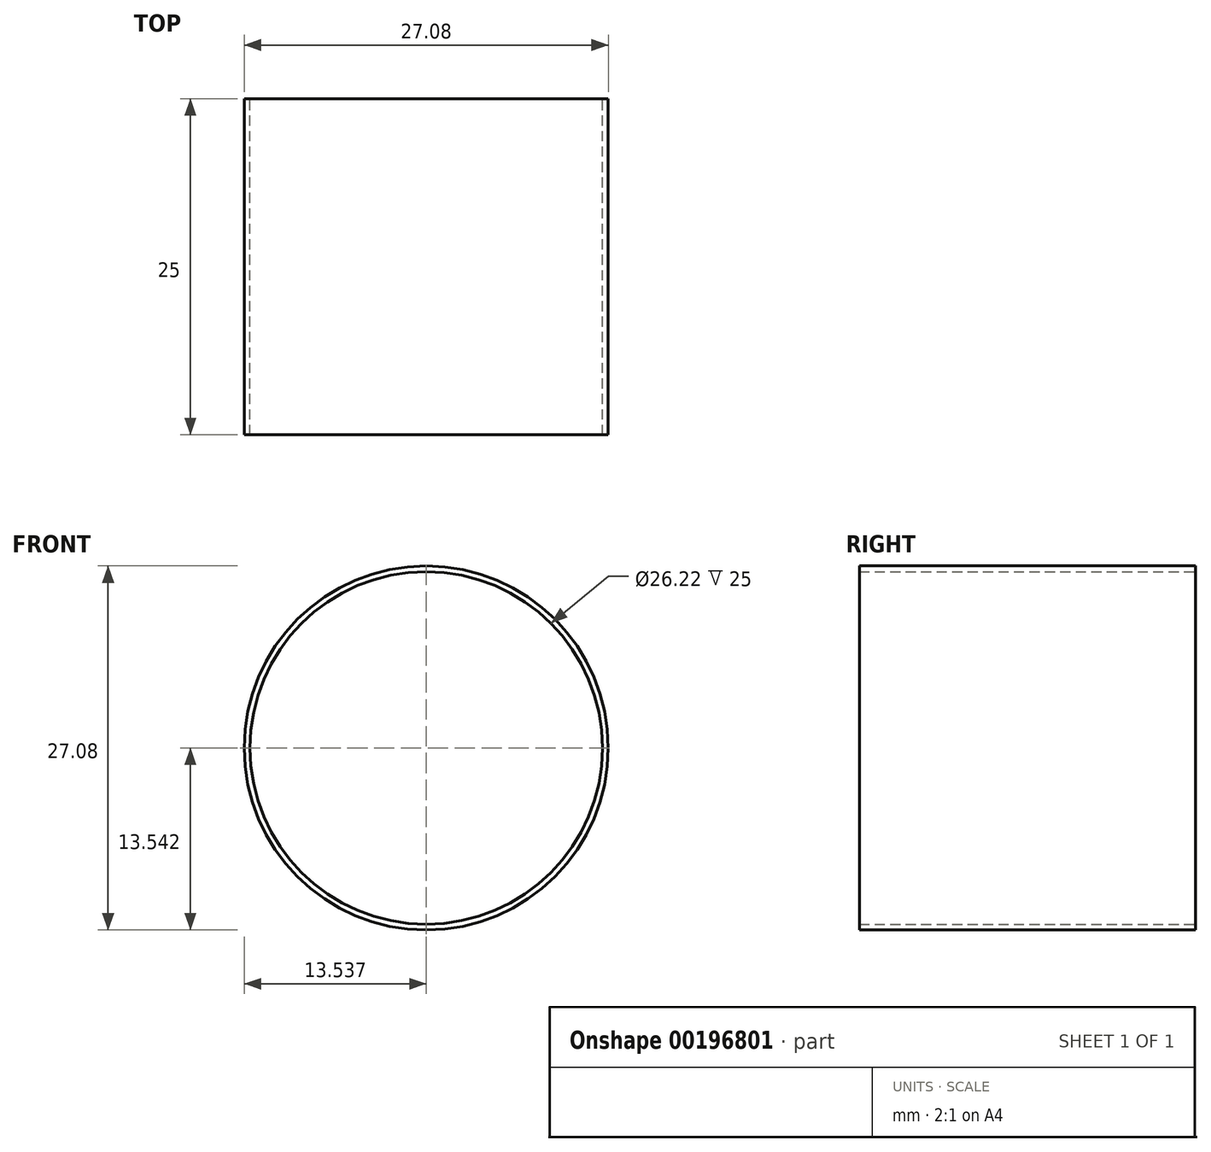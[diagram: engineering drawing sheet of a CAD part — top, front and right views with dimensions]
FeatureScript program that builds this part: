
annotation { "Feature Type Name" : "Feature", "Feature Type Description" : "" }
export const myFeature = defineFeature(function(context is Context, id is Id, definition is map)
    precondition{}
    {
        {
            var Q0;
            Q0=qCreatedBy(makeId("Front.planeOp"),FACE);
            var sketch = newSketch(context, id + "F0", { "sketchPlane" : qUnion([Q0])});
            skCircle(sketch, "E0", {"center": v(-43.53, 11.36) * mm, "radius": 13.54 * mm});
            skCircle(sketch, "E1", {"center": v(-43.53, 11.36) * mm, "radius": 13.1 * mm});
            skSolve(sketch);
        }
        {
            var Q0;
            Q0 = qSketchRegion(id + "F0", true);
            extrude(context, id + "F1", {"entities" : qUnion([Q0]), "depth" : 25 * mm});
        }
    });
